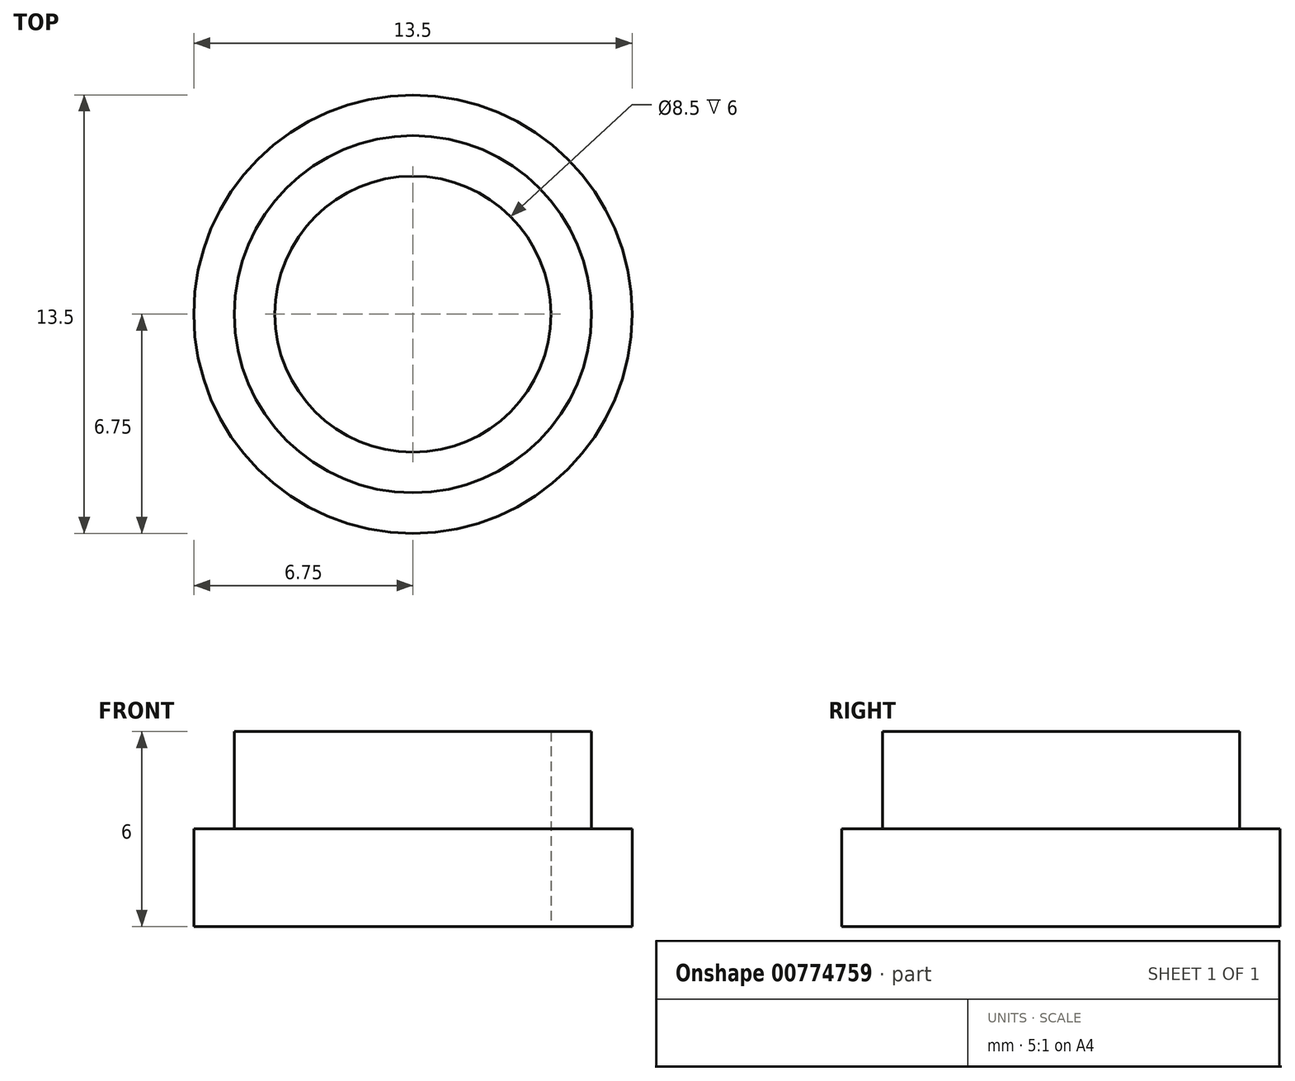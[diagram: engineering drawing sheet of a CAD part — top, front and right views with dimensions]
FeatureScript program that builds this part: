
annotation { "Feature Type Name" : "Feature", "Feature Type Description" : "" }
export const myFeature = defineFeature(function(context is Context, id is Id, definition is map)
    precondition{}
    {
        {
            assignVariable(context, id + "F0", {"name" : "SpacerH", "anyValue" : 6});
        }
        {
            assignVariable(context, id + "F1", {"name" : "SpacerStepH", "anyValue" : 3});
        }
        {
            var Q0;
            Q0=qCreatedBy(makeId("Top.planeOp"),FACE);
            var sketch = newSketch(context, id + "F2", { "sketchPlane" : qUnion([Q0])});
            skCircle(sketch, "E0", {"center": v(0, 0) * mm, "radius": 4.25 * mm});
            skCircle(sketch, "E1", {"center": v(0, 0) * mm, "radius": 5.5 * mm});
            skCircle(sketch, "E2", {"center": v(0, 0) * mm, "radius": 6.75 * mm});
            skSolve(sketch);
        }
        {
            var Q0;
            Q0=makeQuery(id+"F2.imprint","IMPRINT",FACE,{"disambiguationData":[TD([[makeQuery(id+"F2.imprint","IMPRINT",EDGE,{"derivedFrom":sQuery(id+"F2.wireOp",EDGE,"E0")}),-1.0]])]});
            extrude(context, id + "F3", {"entities" : qUnion([Q0]), "depth" : (getVariable(context, 'SpacerH')) * mm, "offsetDistance" : 25 * mm});
        }
        {
            var Q0;
            Q0 = qSketchRegion(id + "F2", true);
            extrude(context, id + "F4", {"entities" : qUnion([Q0]), "operationType" : NewBodyOperationType.ADD, "depth" : (getVariable(context, 'SpacerStepH')) * mm, "offsetDistance" : 25 * mm});
        }
    });
